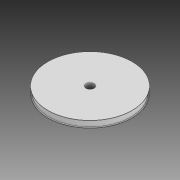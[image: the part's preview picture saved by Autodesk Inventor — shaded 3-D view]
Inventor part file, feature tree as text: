
AUTODESK INVENTOR PART (.ipt)
format: ipt  version: 2020 (Build 240168000, 168)  size: 98,304 bytes
history: native  units: mm
features: revolve x1, sketch x1
ambient origin geometry x8: Origin, YZ Plane, XZ Plane, XY Plane, X Axis, Y Axis, Z Axis, Center Point
bodies: Solid1 (feature_tree)
feature tree (2):
  revolve  "Revolution1"  [1 undecoded]
  sketch  "Sketch1"  dims[d0=100.0mm d1=15.0mm d2=1.0mm d3=1.0mm d4=10.0mm d5=3.0mm d6=90.0deg]
note: 1 required parameter value undecoded (feature->parameter linkage not recoverable at this tier; creation-order binding heuristic only, values carry confidence <= 0.55)
